annotation { "Feature Type Name" : "Feature", "Feature Type Description" : "" }
export const myFeature = defineFeature(function(context is Context, id is Id, definition is map)
    precondition{}
    {
        {
            var Q0;
            Q0=qCreatedBy(makeId("Front.planeOp"),FACE);
            var sketch = newSketch(context, id + "F0", { "sketchPlane" : qUnion([Q0])});
            skLineSegment(sketch, "E0.bottom", {"start": v(381, 177.8) * mm, "end": v(-381, 177.8) * mm});
            skLineSegment(sketch, "E0.top", {"start": v(381, -177.8) * mm, "end": v(-381, -177.8) * mm});
            skLineSegment(sketch, "E0.left", {"start": v(381, 177.8) * mm, "end": v(381, -177.8) * mm});
            skLineSegment(sketch, "E0.right", {"start": v(-381, 177.8) * mm, "end": v(-381, -177.8) * mm});
            skPoint(sketch, "E0.middle", {"position": v(0, 0) * mm});
            skLineSegment(sketch, "E1", {"start": v(-381, 177.8) * mm, "end": v(-381, 330.2) * mm});
            skLineSegment(sketch, "E2", {"start": v(-381, 330.2) * mm, "end": v(381, 330.2) * mm});
            skLineSegment(sketch, "E3", {"start": v(381, 330.2) * mm, "end": v(381, 177.8) * mm});
            skSolve(sketch);
        }
        {
            var Q0;
            Q0=makeQuery(id+"F0.imprint","IMPRINT",FACE,{"disambiguationData":[TD([[makeQuery(id+"F0.imprint","IMPRINT",EDGE,{"derivedFrom":sQuery(id+"F0.wireOp",EDGE,"E0.bottom")}),1.0]])]});
            extrude(context, id + "F1", {"entities" : qUnion([Q0]), "depth" : 50.8 * mm});
        }
        {
            var Q0;
            Q0=makeQuery(id+"F1.opExtrude","CAP_FACE",FACE,{"disambiguationData":[OSD([sQuery(id+"F0.wireOp",EDGE,"E0.bottom"),sQuery(id+"F0.wireOp",EDGE,"E0.top"),sQuery(id+"F0.wireOp",EDGE,"E0.left"),sQuery(id+"F0.wireOp",EDGE,"E0.right")])],"isStart":false});
            var sketch = newSketch(context, id + "F2", { "sketchPlane" : qUnion([Q0])});
            skPoint(sketch, "E4.startSnap0", {"position": v(68.17, -37.6) * mm});
            skLineSegment(sketch, "E5.bottom", {"start": v(302.26, -108.5) * mm, "end": v(64.05, -108.5) * mm});
            skLineSegment(sketch, "E5.top", {"start": v(302.26, -146.6) * mm, "end": v(64.05, -146.6) * mm});
            skLineSegment(sketch, "E5.left", {"start": v(342.9, -108.5) * mm, "end": v(342.9, -146.6) * mm});
            skLineSegment(sketch, "E5.right", {"start": v(-342.9, -108.5) * mm, "end": v(-342.9, -146.6) * mm});
            skPoint(sketch, "E5.middle", {"position": v(0, -127.54) * mm});
            skEllipticalArc(sketch, "E6", {});
            skLineSegment(sketch, "E7.trimOffspring", {"start": v(-64.05, -108.5) * mm, "end": v(-342.9, -108.5) * mm});
            skLineSegment(sketch, "E8.trimOffspring", {"start": v(-64.05, -146.6) * mm, "end": v(-342.9, -146.6) * mm});
            skEllipticalArc(sketch, "E9.trimOffspring", {});
            skLineSegment(sketch, "E10.bottom", {"start": v(274.54, 35.42) * mm, "end": v(242.8, 35.42) * mm});
            skLineSegment(sketch, "E10.top", {"start": v(274.54, -59.83) * mm, "end": v(242.8, -59.83) * mm});
            skLineSegment(sketch, "E10.left", {"start": v(274.54, 35.42) * mm, "end": v(274.54, 3.8) * mm});
            skLineSegment(sketch, "E10.right", {"start": v(242.8, 35.42) * mm, "end": v(242.8, 3.8) * mm});
            skPoint(sketch, "E10.middle", {"position": v(258.67, -12.2) * mm});
            skLineSegment(sketch, "E11.bottom", {"start": v(211.04, 35.42) * mm, "end": v(179.3, 35.42) * mm});
            skLineSegment(sketch, "E11.top", {"start": v(211.04, -59.83) * mm, "end": v(179.3, -59.83) * mm});
            skLineSegment(sketch, "E11.left", {"start": v(211.04, 35.42) * mm, "end": v(211.04, 22.85) * mm});
            skLineSegment(sketch, "E11.right", {"start": v(179.3, 35.42) * mm, "end": v(179.3, 23.48) * mm});
            skPoint(sketch, "E11.middle", {"position": v(195.17, -12.2) * mm});
            skLineSegment(sketch, "E12.trimOffspring", {"start": v(179.3, -49.54) * mm, "end": v(179.3, -59.83) * mm});
            skLineSegment(sketch, "E13.trimOffspring", {"start": v(211.04, -49.54) * mm, "end": v(211.04, -59.83) * mm});
            skLineSegment(sketch, "E14.trimOffspring", {"start": v(242.8, -30.49) * mm, "end": v(242.8, -59.83) * mm});
            skLineSegment(sketch, "E15.trimOffspring", {"start": v(274.54, -30.49) * mm, "end": v(274.54, -59.83) * mm});
            skLineSegment(sketch, "E16.bottom", {"start": v(151.99, -9.03) * mm, "end": v(111.35, -9.03) * mm});
            skLineSegment(sketch, "E16.top", {"start": v(151.99, -59.83) * mm, "end": v(111.35, -59.83) * mm});
            skLineSegment(sketch, "E16.left", {"start": v(151.99, -9.03) * mm, "end": v(151.99, -29.18) * mm});
            skLineSegment(sketch, "E16.right", {"start": v(111.35, -9.03) * mm, "end": v(111.35, -29.18) * mm});
            skPoint(sketch, "E16.middle", {"position": v(131.67, -34.43) * mm});
            skLineSegment(sketch, "E17.bottom", {"start": v(87.22, -15.38) * mm, "end": v(49.12, -15.38) * mm});
            skLineSegment(sketch, "E17.top", {"start": v(87.22, -59.83) * mm, "end": v(49.12, -59.83) * mm});
            skLineSegment(sketch, "E17.left", {"start": v(87.22, -15.38) * mm, "end": v(87.22, -29.28) * mm});
            skLineSegment(sketch, "E17.right", {"start": v(49.12, -15.38) * mm, "end": v(49.12, -29.28) * mm});
            skLineSegment(sketch, "E18.trimOffspring", {"start": v(49.12, -55.12) * mm, "end": v(49.12, -59.83) * mm});
            skLineSegment(sketch, "E19.trimOffspring", {"start": v(87.22, -48.21) * mm, "end": v(87.22, -59.83) * mm});
            skLineSegment(sketch, "E20.trimOffspring", {"start": v(111.35, -47.04) * mm, "end": v(111.35, -59.83) * mm});
            skLineSegment(sketch, "E21.trimOffspring", {"start": v(151.99, -47.04) * mm, "end": v(151.99, -59.83) * mm});
            skLineSegment(sketch, "E22.bottom", {"start": v(302.26, -146.6) * mm, "end": v(342.9, -146.6) * mm});
            skLineSegment(sketch, "E22.top", {"start": v(302.26, -80.55) * mm, "end": v(342.9, -80.55) * mm});
            skLineSegment(sketch, "E22.left", {"start": v(302.26, -108.5) * mm, "end": v(302.26, -80.55) * mm});
            skLineSegment(sketch, "E22.right", {"start": v(342.9, -146.6) * mm, "end": v(342.9, -80.55) * mm});
            skLineSegment(sketch, "E23", {"start": v(179.3, 23.48) * mm, "end": v(179.3, -1.93) * mm});
            skLineSegment(sketch, "E24", {"start": v(211.04, 22.85) * mm, "end": v(211.04, -1.93) * mm});
            skLineSegment(sketch, "E25", {"start": v(242.8, 3.8) * mm, "end": v(242.8, -1.93) * mm});
            skLineSegment(sketch, "E26", {"start": v(274.54, 3.8) * mm, "end": v(274.54, -1.93) * mm});
            skLineSegment(sketch, "E27.trimOffspring", {"start": v(179.3, -24.77) * mm, "end": v(179.3, -49.54) * mm});
            skLineSegment(sketch, "E28.trimOffspring", {"start": v(211.04, -24.77) * mm, "end": v(211.04, -49.54) * mm});
            skLineSegment(sketch, "E29.trimOffspring", {"start": v(274.54, -24.77) * mm, "end": v(274.54, -30.49) * mm});
            skLineSegment(sketch, "E30.trimOffspring", {"start": v(242.8, -24.77) * mm, "end": v(242.8, -30.49) * mm});
            skLineSegment(sketch, "E31", {"start": v(316.03, 118.22) * mm, "end": v(316.03, 136) * mm});
            skCircle(sketch, "E32", {"center": v(316.03, 136) * mm, "radius": 17.78 * mm});
            skArc(sketch, "E33", {"start": v(325.55, 99.1) * mm, "mid": v(341.96, 108.1) * mm, "end": v(352.12, 123.8) * mm});
            skLineSegment(sketch, "E34", {"start": v(316.03, 70.53) * mm, "end": v(306.5, 70.53) * mm});
            skLineSegment(sketch, "E35.bottom", {"start": v(306.5, 70.53) * mm, "end": v(325.55, 70.53) * mm});
            skLineSegment(sketch, "E35.left", {"start": v(306.5, 19.05) * mm, "end": v(306.5, 70.53) * mm});
            skLineSegment(sketch, "E35.right", {"start": v(325.55, 19.05) * mm, "end": v(325.55, 70.53) * mm});
            skLineSegment(sketch, "E36", {"start": v(306.5, 70.53) * mm, "end": v(306.5, 99.1) * mm});
            skLineSegment(sketch, "E37", {"start": v(325.55, 70.53) * mm, "end": v(325.55, 99.1) * mm});
            skCircle(sketch, "E38", {"center": v(213.4, 136) * mm, "radius": 17.78 * mm});
            skArc(sketch, "E39", {"start": v(222.93, 99.1) * mm, "mid": v(239.34, 108.1) * mm, "end": v(249.5, 123.8) * mm});
            skLineSegment(sketch, "E40", {"start": v(213.4, 70.53) * mm, "end": v(203.88, 70.53) * mm});
            skLineSegment(sketch, "E41.bottom", {"start": v(203.88, 70.53) * mm, "end": v(222.93, 70.53) * mm});
            skLineSegment(sketch, "E41.left", {"start": v(203.88, 70.53) * mm, "end": v(203.88, 99.1) * mm});
            skLineSegment(sketch, "E41.right", {"start": v(222.93, 70.53) * mm, "end": v(222.93, 99.1) * mm});
            skEllipticalArc(sketch, "E42", {});
            skEllipticalArc(sketch, "E43", {});
            skArc(sketch, "E44.trimOffspring", {"start": v(177.31, 123.8) * mm, "mid": v(187.47, 108.1) * mm, "end": v(203.88, 99.1) * mm});
            skEllipticalArc(sketch, "E45.trimOffspring", {});
            skArc(sketch, "E46.trimOffspring", {"start": v(249.5, 148.2) * mm, "mid": v(213.4, 174.1) * mm, "end": v(177.31, 148.2) * mm});
            skArc(sketch, "E47.trimOffspring", {"start": v(279.93, 123.8) * mm, "mid": v(290.09, 108.1) * mm, "end": v(306.5, 99.1) * mm});
            skArc(sketch, "E48.trimOffspring", {"start": v(352.12, 148.2) * mm, "mid": v(316.03, 174.1) * mm, "end": v(279.93, 148.2) * mm});
            skEllipticalArc(sketch, "E49.trimOffspring", {});
            skLineSegment(sketch, "E50", {"start": v(49.12, -29.28) * mm, "end": v(49.12, -55.12) * mm});
            skLineSegment(sketch, "E51", {"start": v(87.22, -48.21) * mm, "end": v(87.22, -29.28) * mm});
            skLineSegment(sketch, "E52", {"start": v(111.35, -29.18) * mm, "end": v(111.35, -47.04) * mm});
            skLineSegment(sketch, "E53", {"start": v(151.99, -47.04) * mm, "end": v(151.99, -29.18) * mm});
            skLineSegment(sketch, "E54", {"start": v(179.3, -24.77) * mm, "end": v(179.3, -1.93) * mm});
            skLineSegment(sketch, "E55", {"start": v(211.04, -1.93) * mm, "end": v(211.04, -24.77) * mm});
            skLineSegment(sketch, "E56", {"start": v(242.8, -1.93) * mm, "end": v(242.8, -24.77) * mm});
            skLineSegment(sketch, "E57", {"start": v(274.54, -24.77) * mm, "end": v(274.54, -1.93) * mm});
            skLineSegment(sketch, "E58", {"start": v(68.17, -15.38) * mm, "end": v(68.17, -59.83) * mm});
            skLineSegment(sketch, "E59", {"start": v(195.17, 35.42) * mm, "end": v(195.17, -59.83) * mm});
            skLineSegment(sketch, "E60", {"start": v(258.67, 35.42) * mm, "end": v(258.67, -59.83) * mm});
            skLineSegment(sketch, "E61", {"start": v(322.58, -80.55) * mm, "end": v(322.58, -146.6) * mm});
            skLineSegment(sketch, "E62.bottom", {"start": v(144.37, 54.47) * mm, "end": v(118.97, 54.47) * mm});
            skLineSegment(sketch, "E62.left", {"start": v(144.37, 54.47) * mm, "end": v(144.37, -9.03) * mm});
            skLineSegment(sketch, "E62.right", {"start": v(118.97, 54.47) * mm, "end": v(118.97, -9.03) * mm});
            skPoint(sketch, "E62.middle", {"position": v(131.67, -9.03) * mm});
            skLineSegment(sketch, "E63", {"start": v(131.67, 54.47) * mm, "end": v(131.67, -59.83) * mm});
            const initialGuessF2  = {"E6": [0, -0.12754330039024353, 0, 1, 0.03175, 0.08005957150459891, 2.2142974355881817, 4.068887871591417], "E9.trimOffspring": [0, -0.12754330039024353, 0, 1, 0.03175, 0.08005957150459891, 5.355890089177974, 0.9272952180015617], "E42": [0.21340733613073826, 0.13599922996163366, -1, 0, 0.04699, 0.01905, 5.588315915252005, 0.6948693919275802], "E43": [0.3160264520794153, 0.13599922996163377, 1, 0, 0.04699, 0.01905, 2.446723261662213, 3.8364620455173712], "E45.trimOffspring": [0.21340733613073826, 0.13599922996163366, -1, 0, 0.04699, 0.01905, 2.4467232616622128, 3.8364620455173735], "E49.trimOffspring": [0.3160264520794153, 0.13599922996163377, 1, 0, 0.04699, 0.01905, 5.588315915252006, 0.6948693919275803]};
            skSetInitialGuess(sketch, initialGuessF2);
            skSolve(sketch);
        }
        {
            var Q0;
            Q0=makeQuery(id+"F2.imprint","IMPRINT",FACE,{"disambiguationData":[TD([[makeQuery(id+"F2.imprint","IMPRINT",EDGE,{"derivedFrom":sQuery(id+"F2.wireOp",EDGE,"E5.bottom")}),1.0]])]});
            var Q1;
            Q1=makeQuery(id+"F2.imprint","IMPRINT",FACE,{"disambiguationData":[TD([[makeQuery(id+"F2.imprint","IMPRINT",EDGE,{"derivedFrom":sQuery(id+"F2.wireOp",EDGE,"E32")}),-1.0]])]});
            var Q2;
            Q2=makeQuery(id+"F2.imprint","IMPRINT",FACE,{"disambiguationData":[TD([[makeQuery(id+"F2.imprint","IMPRINT",EDGE,{"derivedFrom":sQuery(id+"F2.wireOp",EDGE,"E38")}),-1.0]])]});
            var Q3;
            Q3=makeQuery(id+"F2.imprint","IMPRINT",FACE,{"disambiguationData":[TD([[makeQuery(id+"F2.imprint","IMPRINT",EDGE,{"derivedFrom":sQuery(id+"F2.wireOp",EDGE,"E5.bottom")}),1.0]])]});
            var Q4;
            {var subQ6=sQuery(id+"F2.wireOp",EDGE,"E61");Q4=makeQuery(id+"F2.imprint","IMPRINT",FACE,{"disambiguationData":[TD([[makeQuery(id+"F2.imprint","IMPRINT",EDGE,{"derivedFrom":subQ6}),1.0]])]});}
            extrude(context, id + "F3", {"entities" : qUnion([Q0, Q1, Q2, Q3, Q4]), "operationType" : NewBodyOperationType.REMOVE, "oppositeDirection" : true, "depth" : 25.4 * mm});
        }
        {
            var Q0;
            {var subQ0=sQuery(id+"F0.wireOp",EDGE,"E0.top");var subQ1=sQuery(id+"F0.wireOp",EDGE,"E0.right");var subQ2=sQuery(id+"F0.wireOp",EDGE,"E0.bottom");var subQ3=sQuery(id+"F0.wireOp",EDGE,"E0.left");Q0=makeQuery(id+"F3.boolean.opBoolean","SPLIT",FACE,{"disambiguationData":[TD([makeQuery(id+"F1.opExtrude","SWEPT_FACE",FACE,{"disambiguationData":[OSD([subQ2])]})])],"derivedFrom":makeQuery(id+"F1.opExtrude","CAP_FACE",FACE,{"disambiguationData":[OSD([subQ2,subQ0,subQ3,subQ1])],"isStart":false})});}
            var sketch = newSketch(context, id + "F4", { "sketchPlane" : qUnion([Q0])});
            skArc(sketch, "E64", {"start": v(41.9, 112.87) * mm, "mid": v(91.74, 71.9) * mm, "end": v(141.58, 112.87) * mm});
            skCircle(sketch, "E65.cCircle", {"center": v(91.74, 122.7) * mm, "radius": 14.29 * mm, "construction": true});
            skLineSegment(sketch, "E65.0", {"start": v(100, 136.99) * mm, "end": v(108.24, 122.69) * mm});
            skLineSegment(sketch, "E65.1", {"start": v(108.24, 122.69) * mm, "end": v(99.97, 108.41) * mm});
            skLineSegment(sketch, "E65.2", {"start": v(99.97, 108.41) * mm, "end": v(83.47, 108.43) * mm});
            skLineSegment(sketch, "E65.3", {"start": v(83.47, 108.43) * mm, "end": v(75.24, 122.73) * mm});
            skLineSegment(sketch, "E65.4", {"start": v(75.24, 122.73) * mm, "end": v(83.5, 137) * mm});
            skLineSegment(sketch, "E65.5", {"start": v(83.5, 137) * mm, "end": v(100, 136.99) * mm});
            skEllipticalArc(sketch, "E66", {});
            skEllipticalArc(sketch, "E67.trimOffspring", {});
            skArc(sketch, "E68.trimOffspring", {"start": v(141.58, 132.55) * mm, "mid": v(91.74, 173.5) * mm, "end": v(41.9, 132.55) * mm});
            const initialGuessF4  = {"E66": [0.09174057850272076, 0.12270955847632314, 1, 0, 0.0635, 0.015875, 2.4732611299189893, 3.809924177260596], "E67.trimOffspring": [0.09174057850272076, 0.12270955847632314, 1, 0, 0.0635, 0.015875, 5.614853783508782, 0.668331523670802]};
            skSetInitialGuess(sketch, initialGuessF4);
            skSolve(sketch);
        }
        {
            var Q0;
            Q0=makeQuery(id+"F0.imprint","IMPRINT",FACE,{"disambiguationData":[TD([[makeQuery(id+"F0.imprint","IMPRINT",EDGE,{"derivedFrom":sQuery(id+"F0.wireOp",EDGE,"E0.bottom")}),-1.0]])]});
            extrude(context, id + "F5", {"entities" : qUnion([Q0]), "operationType" : NewBodyOperationType.ADD, "depth" : 50.8 * mm});
        }
        {
            var Q0;
            {var subQ0=sQuery(id+"F0.wireOp",EDGE,"E0.bottom");var subQ1=sQuery(id+"F0.wireOp",EDGE,"E0.top");var subQ2=sQuery(id+"F0.wireOp",EDGE,"E0.right");var subQ3=sQuery(id+"F0.wireOp",EDGE,"E0.left");Q0=makeQuery(id+"F5.boolean.opBoolean","MERGE",FACE,{"derivedFrom":[makeQuery(id+"F3.boolean.opBoolean","SPLIT",FACE,{"disambiguationData":[TD([makeQuery(id+"F1.opExtrude","SWEPT_FACE",FACE,{"disambiguationData":[OSD([subQ0])]})])],"derivedFrom":makeQuery(id+"F1.opExtrude","CAP_FACE",FACE,{"disambiguationData":[OSD([subQ0,subQ1,subQ3,subQ2])],"isStart":false})}),makeQuery(id+"F5.opExtrude","CAP_FACE",FACE,{"disambiguationData":[OSD([subQ0,sQuery(id+"F0.wireOp",EDGE,"E1"),sQuery(id+"F0.wireOp",EDGE,"E2"),sQuery(id+"F0.wireOp",EDGE,"E3")])],"isStart":false})]});}
            var sketch = newSketch(context, id + "F6", { "sketchPlane" : qUnion([Q0])});
            skArc(sketch, "E69", {"start": v(-118.23, 89.4) * mm, "mid": v(-117.48, 86.16) * mm, "end": v(-116.52, 82.98) * mm});
            skCircle(sketch, "E70.cCircle", {"center": v(-68.4, 99.23) * mm, "radius": 14.29 * mm, "construction": true});
            skLineSegment(sketch, "E70.0", {"start": v(-60.12, 113.5) * mm, "end": v(-51.9, 99.2) * mm});
            skLineSegment(sketch, "E70.1", {"start": v(-51.9, 99.2) * mm, "end": v(-60.16, 84.93) * mm});
            skLineSegment(sketch, "E70.2", {"start": v(-60.16, 84.93) * mm, "end": v(-76.66, 84.95) * mm});
            skLineSegment(sketch, "E70.3", {"start": v(-76.66, 84.95) * mm, "end": v(-84.89, 99.25) * mm});
            skLineSegment(sketch, "E70.4", {"start": v(-84.89, 99.25) * mm, "end": v(-76.62, 113.53) * mm});
            skLineSegment(sketch, "E70.5", {"start": v(-76.62, 113.53) * mm, "end": v(-60.12, 113.5) * mm});
            skPoint(sketch, "E70.0.midPoint", {"position": v(-56, 106.36) * mm});
            skEllipticalArc(sketch, "E71", {});
            skEllipticalArc(sketch, "E72.trimOffspring", {});
            skArc(sketch, "E73.trimOffspring", {"start": v(-18.55, 109.07) * mm, "mid": v(-32.41, 135.1) * mm, "end": v(-58.4, 149.04) * mm});
            skLineSegment(sketch, "E74", {"start": v(-68.4, 99.23) * mm, "end": v(-68.4, 113.52) * mm});
            skLineSegment(sketch, "E75", {"start": v(-68.56, 204) * mm, "end": v(-58.4, 204) * mm});
            skLineSegment(sketch, "E76", {"start": v(-68.56, 204) * mm, "end": v(-78.72, 204) * mm});
            skLineSegment(sketch, "E77", {"start": v(-78.72, 204) * mm, "end": v(-78.72, 148.97) * mm});
            skLineSegment(sketch, "E78", {"start": v(-58.4, 204) * mm, "end": v(-58.4, 149.04) * mm});
            skArc(sketch, "E79.trimOffspring", {"start": v(-78.72, 148.97) * mm, "mid": v(-104.49, 134.97) * mm, "end": v(-118.23, 109.07) * mm});
            skLineSegment(sketch, "E80.1.0", {"start": v(-153.96, 37.9) * mm, "end": v(-106.3, 65.41) * mm});
            skLineSegment(sketch, "E80.1.1", {"start": v(-159.04, 46.7) * mm, "end": v(-164.12, 55.5) * mm});
            skLineSegment(sketch, "E80.1.2", {"start": v(-159.04, 46.7) * mm, "end": v(-153.96, 37.9) * mm});
            skLineSegment(sketch, "E80.1.3", {"start": v(-164.12, 55.5) * mm, "end": v(-116.52, 82.98) * mm});
            skLineSegment(sketch, "E80.2.0", {"start": v(27.51, 55.79) * mm, "end": v(-20.15, 83.3) * mm});
            skLineSegment(sketch, "E80.2.1", {"start": v(22.43, 46.99) * mm, "end": v(17.35, 38.19) * mm});
            skLineSegment(sketch, "E80.2.2", {"start": v(22.43, 46.99) * mm, "end": v(27.51, 55.79) * mm});
            skLineSegment(sketch, "E80.2.3", {"start": v(17.35, 38.19) * mm, "end": v(-30.25, 65.67) * mm});
            skArc(sketch, "E81.trimOffspring", {"start": v(-20.15, 83.3) * mm, "mid": v(-19.26, 86.32) * mm, "end": v(-18.55, 89.4) * mm});
            skArc(sketch, "E82.trimOffspring", {"start": v(-106.3, 65.41) * mm, "mid": v(-68.22, 48.43) * mm, "end": v(-30.25, 65.67) * mm});
            skLineSegment(sketch, "E83.bottom", {"start": v(-352.23, 206.96) * mm, "end": v(-218.88, 206.96) * mm});
            skLineSegment(sketch, "E83.top", {"start": v(-320.48, -47.04) * mm, "end": v(-206.18, -47.04) * mm});
            skLineSegment(sketch, "E83.left", {"start": v(-352.23, 200.6) * mm, "end": v(-352.23, 124.4) * mm});
            skLineSegment(sketch, "E84", {"start": v(-352.23, 206.96) * mm, "end": v(-352.23, 130.76) * mm});
            skLineSegment(sketch, "E85", {"start": v(-345.88, 124.4) * mm, "end": v(-326.83, 124.4) * mm});
            skLineSegment(sketch, "E86", {"start": v(-320.48, 118.06) * mm, "end": v(-320.48, 38.68) * mm});
            skLineSegment(sketch, "E87", {"start": v(-323.65, 35.5) * mm, "end": v(-323.65, 35.5) * mm});
            skLineSegment(sketch, "E88", {"start": v(-326.83, 32.33) * mm, "end": v(-326.83, -40.7) * mm});
            skLineSegment(sketch, "E89", {"start": v(-326.83, -47.04) * mm, "end": v(-199.83, -47.04) * mm});
            skLineSegment(sketch, "E90", {"start": v(-199.83, -40.7) * mm, "end": v(-199.83, 35.5) * mm});
            skLineSegment(sketch, "E91", {"start": v(-206.18, 41.86) * mm, "end": v(-225.23, 41.86) * mm});
            skLineSegment(sketch, "E92", {"start": v(-231.58, 48.2) * mm, "end": v(-231.58, 118.06) * mm});
            skLineSegment(sketch, "E93", {"start": v(-345.88, 206.96) * mm, "end": v(-218.88, 206.96) * mm});
            skLineSegment(sketch, "E94", {"start": v(-218.88, 133.93) * mm, "end": v(-218.88, 146.63) * mm});
            skLineSegment(sketch, "E95", {"start": v(-231.58, 118.06) * mm, "end": v(-218.88, 133.93) * mm});
            skLineSegment(sketch, "E96", {"start": v(-218.88, 146.63) * mm, "end": v(-196.65, 155.52) * mm});
            skLineSegment(sketch, "E97", {"start": v(-218.88, 206.96) * mm, "end": v(-196.65, 198.07) * mm});
            skLineSegment(sketch, "E98", {"start": v(-196.65, 198.07) * mm, "end": v(-196.65, 184.73) * mm});
            skLineSegment(sketch, "E99.bottom", {"start": v(-196.65, 184.73) * mm, "end": v(-164.9, 184.73) * mm});
            skLineSegment(sketch, "E99.top", {"start": v(-196.65, 168.86) * mm, "end": v(-164.9, 168.86) * mm});
            skLineSegment(sketch, "E99.right", {"start": v(-164.9, 184.73) * mm, "end": v(-164.9, 168.86) * mm});
            skLineSegment(sketch, "E100.trimOffspring", {"start": v(-196.65, 168.86) * mm, "end": v(-196.65, 155.52) * mm});
            skPoint(sketch, "E101.visualSharp", {"position": v(-352.23, 206.96) * mm});
            skArc(sketch, "E101.filletArc", {"start": v(-345.88, 206.96) * mm, "mid": v(-350.37, 205.1) * mm, "end": v(-352.23, 200.6) * mm});
            skPoint(sketch, "E102.visualSharp", {"position": v(-352.23, 124.4) * mm});
            skArc(sketch, "E102.filletArc", {"start": v(-352.23, 130.76) * mm, "mid": v(-350.37, 126.27) * mm, "end": v(-345.88, 124.4) * mm});
            skPoint(sketch, "E103.visualSharp", {"position": v(-320.48, 124.4) * mm});
            skArc(sketch, "E103.filletArc", {"start": v(-320.48, 118.06) * mm, "mid": v(-322.34, 122.55) * mm, "end": v(-326.83, 124.4) * mm});
            skPoint(sketch, "E104.visualSharp", {"position": v(-231.58, 41.86) * mm});
            skArc(sketch, "E104.filletArc", {"start": v(-231.58, 48.2) * mm, "mid": v(-229.72, 43.72) * mm, "end": v(-225.23, 41.86) * mm});
            skPoint(sketch, "E105.visualSharp", {"position": v(-199.83, 41.86) * mm});
            skArc(sketch, "E105.filletArc", {"start": v(-199.83, 35.5) * mm, "mid": v(-201.69, 40) * mm, "end": v(-206.18, 41.86) * mm});
            skPoint(sketch, "E106.visualSharp", {"position": v(-326.83, -47.04) * mm});
            skArc(sketch, "E106.filletArc", {"start": v(-326.83, -40.7) * mm, "mid": v(-324.97, -45.18) * mm, "end": v(-320.48, -47.04) * mm});
            skPoint(sketch, "E107.visualSharp", {"position": v(-199.83, -47.04) * mm});
            skArc(sketch, "E107.filletArc", {"start": v(-206.18, -47.04) * mm, "mid": v(-201.69, -45.18) * mm, "end": v(-199.83, -40.7) * mm});
            skPoint(sketch, "E108.visualSharp", {"position": v(-320.48, 35.5) * mm});
            skArc(sketch, "E108.filletArc", {"start": v(-323.65, 35.5) * mm, "mid": v(-321.4, 36.44) * mm, "end": v(-320.48, 38.68) * mm});
            skPoint(sketch, "E109.visualSharp", {"position": v(-326.83, 35.5) * mm});
            skArc(sketch, "E109.filletArc", {"start": v(-323.65, 35.5) * mm, "mid": v(-325.9, 34.58) * mm, "end": v(-326.83, 32.33) * mm});
            const initialGuessF6  = {"E71": [-0.06839017023356964, 0.09922866459815055, 1, 0, 0.0635, 0.015875, 2.4732611299189897, 3.8099241772605947], "E72.trimOffspring": [-0.06839017023356964, 0.09922866459815055, 1, 0, 0.0635, 0.015875, 5.6148537835087815, 0.668331523670802]};
            skSetInitialGuess(sketch, initialGuessF6);
            skSolve(sketch);
        }
        {
            var Q0;
            Q0=makeQuery(id+"F6.imprint","IMPRINT",FACE,{"disambiguationData":[TD([[makeQuery(id+"F6.imprint","IMPRINT",EDGE,{"derivedFrom":sQuery(id+"F6.wireOp",EDGE,"E85")}),1.0]])]});
            extrude(context, id + "F7", {"entities" : qUnion([Q0]), "operationType" : NewBodyOperationType.REMOVE, "oppositeDirection" : true, "depth" : 48.26 * mm});
        }
        {
            var Q0;
            Q0=makeQuery(id+"F6.imprint","IMPRINT",FACE,{"disambiguationData":[TD([[makeQuery(id+"F6.imprint","IMPRINT",EDGE,{"derivedFrom":sQuery(id+"F6.wireOp",EDGE,"E69")}),1.0]])]});
            extrude(context, id + "F8", {"entities" : qUnion([Q0]), "operationType" : NewBodyOperationType.REMOVE, "oppositeDirection" : true, "depth" : 6.35 * mm});
        }
        {
            var Q0;
            {var subQ0=sQuery(id+"F6.wireOp",EDGE,"E70.0");Q0=makeQuery(id+"F6.imprint","IMPRINT",FACE,{"disambiguationData":[TD([[makeQuery(id+"F6.imprint","IMPRINT",EDGE,{"derivedFrom":subQ0}),-1.0]])]});}
            extrude(context, id + "F9", {"entities" : qUnion([Q0]), "operationType" : NewBodyOperationType.REMOVE, "oppositeDirection" : true, "depth" : 12.7 * mm});
        }
        {
            var Q0;
            {var subQ2=sQuery(id+"F0.wireOp",EDGE,"E3");var subQ3=sQuery(id+"F0.wireOp",EDGE,"E2");var subQ31=sQuery(id+"F0.wireOp",EDGE,"E1");var subQ38=sQuery(id+"F0.wireOp",EDGE,"E0.right");var subQ41=sQuery(id+"F0.wireOp",EDGE,"E0.left");var subQ62=sQuery(id+"F0.wireOp",EDGE,"E0.top");var subQ63=makeQuery(id+"F1.opExtrude","SWEPT_FACE",FACE,{"disambiguationData":[OSD([subQ62])]});var subQ71=sQuery(id+"F0.wireOp",EDGE,"E0.bottom");Q0=makeQuery(id+"F8.boolean.opBoolean","SPLIT",FACE,{"disambiguationData":[TD([subQ63])],"derivedFrom":makeQuery(id+"F5.boolean.opBoolean","MERGE",FACE,{"derivedFrom":[makeQuery(id+"F3.boolean.opBoolean","SPLIT",FACE,{"disambiguationData":[TD([makeQuery(id+"F1.opExtrude","SWEPT_FACE",FACE,{"disambiguationData":[OSD([subQ71])]})])],"derivedFrom":makeQuery(id+"F1.opExtrude","CAP_FACE",FACE,{"disambiguationData":[OSD([subQ71,subQ62,subQ41,subQ38])],"isStart":false})}),makeQuery(id+"F5.opExtrude","CAP_FACE",FACE,{"disambiguationData":[OSD([subQ71,subQ31,subQ3,subQ2])],"isStart":false})]})});}
            var sketch = newSketch(context, id + "F10", { "sketchPlane" : qUnion([Q0])});
            skLineSegment(sketch, "E110", {"start": v(18.51, -22.83) * mm, "end": v(18.51, -15.21) * mm});
            skLineSegment(sketch, "E111", {"start": v(18.51, -15.21) * mm, "end": v(-65.58, -7.23) * mm});
            skLineSegment(sketch, "E112", {"start": v(18.51, -22.83) * mm, "end": v(-65.58, -30.09) * mm});
            skPoint(sketch, "E113.centerSnap0", {"position": v(-143.46, -18.66) * mm});
            skEllipticalArc(sketch, "E114", {});
            skEllipticalArc(sketch, "E115.trimOffspring", {});
            skEllipse(sketch, "E116", {"center": v(-103.77, -18.66) * mm, "majorRadius": 25.4 * mm, "minorRadius": 12.7 * mm, "majorAxis": v(1, 0)});
            skLineSegment(sketch, "E117", {"start": v(-143.35, -9.04) * mm, "end": v(-143.48, -28.08) * mm});
            skEllipticalArc(sketch, "E118", {});
            skEllipticalArc(sketch, "E119.trimOffspring", {});
            skEllipticalArc(sketch, "E120.trimOffspring", {});
            skEllipticalArc(sketch, "E121.trimOffspring", {});
            skLineSegment(sketch, "E122", {"start": v(18.51, -19.02) * mm, "end": v(12.33, -19.02) * mm});
            const initialGuessF10  = {"E114": [-0.10377129376506507, -0.018655047288672608, 1, 0, 0.04276419384215599, 0.0254, 0.4667653390472961, 1.3303918197278248], "E115.trimOffspring": [-0.10377129376506507, -0.018655047288672608, 1, 0, 0.04276419384215599, 0.0254, 3.5219407379854877, 4.471984473317618], "E118": [-0.10377129376506507, -0.018655047288672608, 1, 0, 0.0127, 0.041275, 0.640613265214955, 2.500979388374838], "E119.trimOffspring": [-0.10377129376506507, -0.018655047288672608, 1, 0, 0.04276419384215599, 0.0254, 1.811200833861968, 2.7531593172365336], "E120.trimOffspring": [-0.10377129376506507, -0.018655047288672608, 1, 0, 0.0127, 0.041275, 3.782205918804747, 5.64257204196463], "E121.trimOffspring": [-0.10377129376506507, -0.018655047288672608, 1, 0, 0.04276419384215599, 0.0254, 4.952793487451761, 5.81641996813229]};
            skSetInitialGuess(sketch, initialGuessF10);
            skSolve(sketch);
        }
        {
            var Q0;
            Q0=makeQuery(id+"F10.imprint","IMPRINT",FACE,{"disambiguationData":[TD([[makeQuery(id+"F10.imprint","IMPRINT",EDGE,{"derivedFrom":sQuery(id+"F10.wireOp",EDGE,"E110")}),1.0]])]});
            extrude(context, id + "F11", {"entities" : qUnion([Q0]), "operationType" : NewBodyOperationType.REMOVE, "oppositeDirection" : true, "depth" : 12.7 * mm});
        }
        {
            var Q0;
            Q0=makeQuery(id+"F4.imprint","IMPRINT",FACE,{"disambiguationData":[TD([[makeQuery(id+"F4.imprint","IMPRINT",EDGE,{"derivedFrom":sQuery(id+"F4.wireOp",EDGE,"E64")}),1.0]])]});
            extrude(context, id + "F12", {"entities" : qUnion([Q0]), "operationType" : NewBodyOperationType.REMOVE, "oppositeDirection" : true, "depth" : 6.35 * mm});
        }
        {
            var Q0;
            {var subQ8=sQuery(id+"F0.wireOp",EDGE,"E1");var subQ17=sQuery(id+"F0.wireOp",EDGE,"E2");var subQ21=sQuery(id+"F0.wireOp",EDGE,"E3");var subQ102=sQuery(id+"F0.wireOp",EDGE,"E0.right");var subQ107=sQuery(id+"F0.wireOp",EDGE,"E0.left");var subQ154=sQuery(id+"F0.wireOp",EDGE,"E0.top");var subQ155=makeQuery(id+"F1.opExtrude","SWEPT_FACE",FACE,{"disambiguationData":[OSD([subQ154])]});var subQ183=sQuery(id+"F0.wireOp",EDGE,"E0.bottom");Q0=makeQuery(id+"F12.boolean.opBoolean","SPLIT",FACE,{"disambiguationData":[TD([makeQuery(id+"F12.opExtrude","SWEPT_FACE",FACE,{"disambiguationData":[OSD([sQuery(id+"F4.wireOp",EDGE,"E65.0")])]})])],"derivedFrom":makeQuery(id+"F11.boolean.opBoolean","SPLIT",FACE,{"disambiguationData":[TD([subQ155])],"derivedFrom":makeQuery(id+"F8.boolean.opBoolean","SPLIT",FACE,{"disambiguationData":[TD([subQ155])],"derivedFrom":makeQuery(id+"F5.boolean.opBoolean","MERGE",FACE,{"derivedFrom":[makeQuery(id+"F3.boolean.opBoolean","SPLIT",FACE,{"disambiguationData":[TD([makeQuery(id+"F1.opExtrude","SWEPT_FACE",FACE,{"disambiguationData":[OSD([subQ183])]})])],"derivedFrom":makeQuery(id+"F1.opExtrude","CAP_FACE",FACE,{"disambiguationData":[OSD([subQ183,subQ154,subQ107,subQ102])],"isStart":false})}),makeQuery(id+"F5.opExtrude","CAP_FACE",FACE,{"disambiguationData":[OSD([subQ183,subQ8,subQ17,subQ21])],"isStart":false})]})})})});}
            extrude(context, id + "F13", {"entities" : qUnion([Q0]), "operationType" : NewBodyOperationType.REMOVE, "oppositeDirection" : true, "depth" : 12.7 * mm});
        }
        {
            var Q0;
            {var subQ11=sQuery(id+"F0.wireOp",EDGE,"E1");var subQ20=sQuery(id+"F0.wireOp",EDGE,"E2");var subQ24=sQuery(id+"F0.wireOp",EDGE,"E3");var subQ108=sQuery(id+"F0.wireOp",EDGE,"E0.right");var subQ113=sQuery(id+"F0.wireOp",EDGE,"E0.left");var subQ163=sQuery(id+"F0.wireOp",EDGE,"E0.top");var subQ164=makeQuery(id+"F1.opExtrude","SWEPT_FACE",FACE,{"disambiguationData":[OSD([subQ163])]});var subQ209=sQuery(id+"F0.wireOp",EDGE,"E0.bottom");Q0=makeQuery(id+"F12.boolean.opBoolean","SPLIT",FACE,{"disambiguationData":[TD([subQ164])],"derivedFrom":makeQuery(id+"F11.boolean.opBoolean","SPLIT",FACE,{"disambiguationData":[TD([subQ164])],"derivedFrom":makeQuery(id+"F8.boolean.opBoolean","SPLIT",FACE,{"disambiguationData":[TD([subQ164])],"derivedFrom":makeQuery(id+"F5.boolean.opBoolean","MERGE",FACE,{"derivedFrom":[makeQuery(id+"F3.boolean.opBoolean","SPLIT",FACE,{"disambiguationData":[TD([makeQuery(id+"F1.opExtrude","SWEPT_FACE",FACE,{"disambiguationData":[OSD([subQ209])]})])],"derivedFrom":makeQuery(id+"F1.opExtrude","CAP_FACE",FACE,{"disambiguationData":[OSD([subQ209,subQ163,subQ113,subQ108])],"isStart":false})}),makeQuery(id+"F5.opExtrude","CAP_FACE",FACE,{"disambiguationData":[OSD([subQ209,subQ11,subQ20,subQ24])],"isStart":false})]})})})});}
            var sketch = newSketch(context, id + "F14", { "sketchPlane" : qUnion([Q0])});
            skText(sketch, "E123", { "text": "Torque Wrench", "fontName": "OpenSans-Regular.ttf"});
            skText(sketch, "E124", { "text": "Needle Nose Pliars", "fontName": "OpenSans-Regular.ttf"});
            skText(sketch, "E125", { "text": "30mm", "fontName": "OpenSans-Regular.ttf"});
            skText(sketch, "E126", { "text": "1-1/8 in", "fontName": "OpenSans-Regular.ttf"});
            skText(sketch, "E127", { "text": "Eye Bolts", "fontName": "OpenSans-Regular.ttf"});
            skLineSegment(sketch, "E128", {"start": v(260.4, 136) * mm, "end": v(269.04, 136) * mm});
            skPoint(sketch, "E129", {"position": v(264.72, 136) * mm});
            skText(sketch, "E130", { "text": "M20X2.5", "fontName": "OpenSans-Regular.ttf"});
            skText(sketch, "E131", { "text": "Tighteners", "fontName": "OpenSans-Regular.ttf"});
            skText(sketch, "E132", { "text": "Impact Wrench", "fontName": "OpenSans-Regular.ttf"});
            const initialGuessF14  = {"E123": [-0.28369, -0.16641, 1, 0, 0.01143], "E124": [-0.1395, -0.08442, 1, 0, 0.01143], "E125": [0.10884, -0.08442, 1, 0, 0.01143], "E126": [0.0377, -0.08442, 1, 0, 0.01143], "E127": [0.22363, 0.18346, 1, 0, 0.01397], "E130": [0.19454, -0.08442, 1, 0, 0.01143], "E131": [-0.0318, 0.18346, 1, 0, 0.01397], "E132": [-0.32682, -0.08442, 1, 0, 0.01143]};
            skSetInitialGuess(sketch, initialGuessF14);
            skSolve(sketch);
        }
        {
            var Q0;
            Q0 = qSketchRegion(id + "F14", true);
            extrude(context, id + "F15", {"entities" : qUnion([Q0]), "operationType" : NewBodyOperationType.REMOVE, "oppositeDirection" : true, "depth" : 3.8 * mm});
        }
        {
            var Q0;
            {var subQ3=sQuery(id+"F2.wireOp",EDGE,"E17.right");Q0=makeQuery(id+"F2.imprint","IMPRINT",FACE,{"disambiguationData":[TD([[makeQuery(id+"F2.imprint","IMPRINT",EDGE,{"derivedFrom":subQ3}),1.0]])]});}
            var Q1;
            Q1=sQuery(id+"F2.wireOp",EDGE,"E58");
            revolve(context, id + "F16", {"operationType" : NewBodyOperationType.REMOVE, "entities" : qUnion([Q0]), "axis" : qUnion([Q1]), "revolveType" : RevolveType.FULL, "oppositeDirection" : true});
        }
        {
            var Q0;
            {var subQ1=sQuery(id+"F2.wireOp",EDGE,"E11.right");Q0=makeQuery(id+"F2.imprint","IMPRINT",FACE,{"disambiguationData":[TD([[makeQuery(id+"F2.imprint","IMPRINT",EDGE,{"derivedFrom":subQ1}),1.0]])]});}
            var Q1;
            Q1=sQuery(id+"F2.wireOp",EDGE,"E59");
            revolve(context, id + "F17", {"operationType" : NewBodyOperationType.REMOVE, "entities" : qUnion([Q0]), "axis" : qUnion([Q1]), "revolveType" : RevolveType.FULL, "oppositeDirection" : true});
        }
        {
            var Q0;
            {var subQ1=sQuery(id+"F2.wireOp",EDGE,"E10.right");Q0=makeQuery(id+"F2.imprint","IMPRINT",FACE,{"disambiguationData":[TD([[makeQuery(id+"F2.imprint","IMPRINT",EDGE,{"derivedFrom":subQ1}),1.0]])]});}
            var Q1;
            Q1=sQuery(id+"F2.wireOp",EDGE,"E60");
            revolve(context, id + "F18", {"operationType" : NewBodyOperationType.REMOVE, "entities" : qUnion([Q0]), "axis" : qUnion([Q1]), "revolveType" : RevolveType.FULL, "oppositeDirection" : true});
        }
        {
            var Q0;
            {var subQ0=sQuery(id+"F0.wireOp",EDGE,"E0.bottom");Q0=makeQuery(id+"F5.boolean.opBoolean","MERGE",FACE,{"derivedFrom":[makeQuery(id+"F1.opExtrude","CAP_FACE",FACE,{"disambiguationData":[OSD([subQ0,sQuery(id+"F0.wireOp",EDGE,"E0.top"),sQuery(id+"F0.wireOp",EDGE,"E0.left"),sQuery(id+"F0.wireOp",EDGE,"E0.right")])],"isStart":true}),makeQuery(id+"F5.opExtrude","CAP_FACE",FACE,{"disambiguationData":[OSD([subQ0,sQuery(id+"F0.wireOp",EDGE,"E1"),sQuery(id+"F0.wireOp",EDGE,"E2"),sQuery(id+"F0.wireOp",EDGE,"E3")])],"isStart":true})]});}
            var sketch = newSketch(context, id + "F19", { "sketchPlane" : qUnion([Q0])});
            skLineSegment(sketch, "E133", {"start": v(0, 0) * mm, "end": v(0, -139.7) * mm});
            skLineSegment(sketch, "E134.bottom", {"start": v(279.4, -123.83) * mm, "end": v(-279.4, -123.82) * mm});
            skLineSegment(sketch, "E134.top", {"start": v(279.4, -155.58) * mm, "end": v(-279.4, -155.57) * mm});
            skPoint(sketch, "E134.middle", {"position": v(0, -139.7) * mm});
            skArc(sketch, "E135", {"start": v(-279.4, -123.82) * mm, "mid": v(-295.28, -139.7) * mm, "end": v(-279.4, -155.57) * mm});
            skArc(sketch, "E136", {"start": v(279.4, -155.58) * mm, "mid": v(295.28, -139.7) * mm, "end": v(279.4, -123.83) * mm});
            skSolve(sketch);
        }
        {
            var Q0;
            Q0 = qSketchRegion(id + "F19", true);
            extrude(context, id + "F20", {"entities" : qUnion([Q0]), "operationType" : NewBodyOperationType.REMOVE, "oppositeDirection" : true, "depth" : 12.7 * mm});
        }
        {
            var Q0;
            {var subQ0=sQuery(id+"F2.wireOp",EDGE,"E16.right");Q0=makeQuery(id+"F2.imprint","IMPRINT",FACE,{"disambiguationData":[TD([[makeQuery(id+"F2.imprint","IMPRINT",EDGE,{"derivedFrom":subQ0}),1.0]])]});}
            var Q1;
            {var subQ0=sQuery(id+"F2.wireOp",EDGE,"E62.right");Q1=makeQuery(id+"F2.imprint","IMPRINT",FACE,{"disambiguationData":[TD([[makeQuery(id+"F2.imprint","IMPRINT",EDGE,{"derivedFrom":subQ0}),1.0]])]});}
            var Q2;
            Q2=sQuery(id+"F2.wireOp",EDGE,"E63");
            revolve(context, id + "F21", {"operationType" : NewBodyOperationType.REMOVE, "entities" : qUnion([Q0, Q1]), "axis" : qUnion([Q2]), "revolveType" : RevolveType.FULL, "oppositeDirection" : true});
        }
        {
            var Q0;
            Q0=makeQuery(id+"F21.boolean.opBoolean","COPY",EDGE,{"derivedFrom":makeQuery(id+"F21.opRevolve","SWEPT_EDGE",EDGE,{"disambiguationData":[OSD([sQuery(id+"F2.wireOp",EDGE,"E16.bottom"),sQuery(id+"F2.wireOp",EDGE,"E62.right")])]})});
            fillet(context, id + "F22", {"entities" : qUnion([Q0]), "radius" : 6.35 * mm, "tangentPropagation" : true, "allowEdgeOverflow" : false});
        }
    });